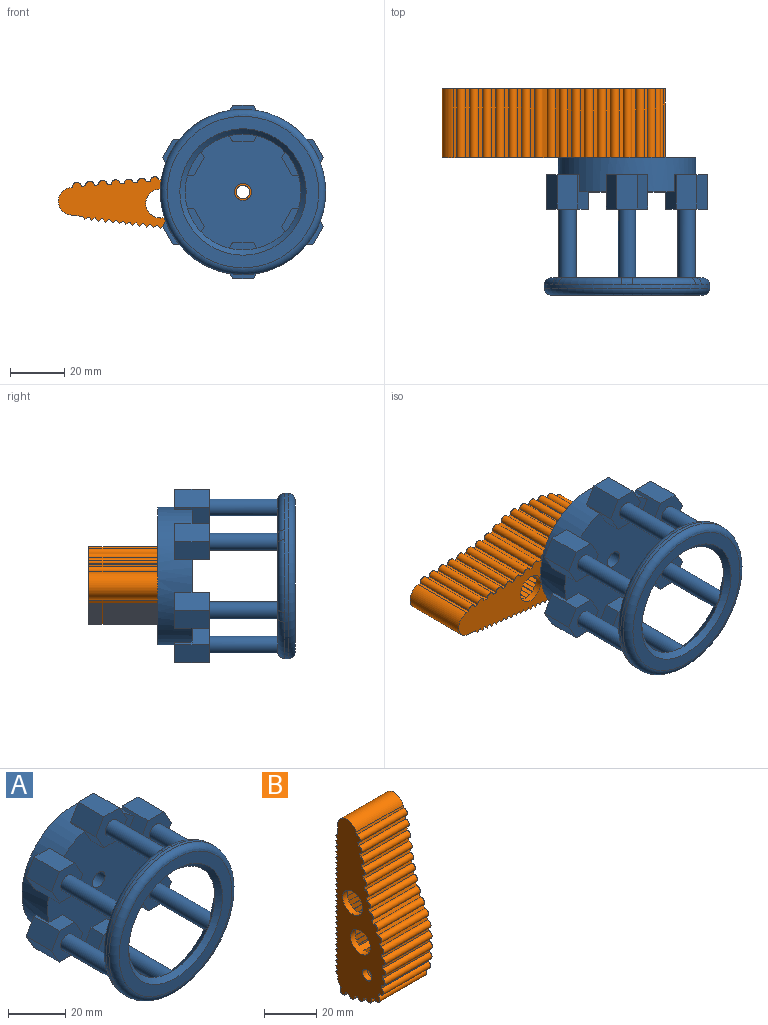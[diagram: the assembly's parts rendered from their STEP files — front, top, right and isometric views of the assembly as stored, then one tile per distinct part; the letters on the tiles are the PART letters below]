
ASSEMBLY  parts=2 mates=1
PART A: 81 faces, bbox 66.1x50.8x66.1 mm
  f0: plane 21.25x12.33mm, normal (0,1,0), area 47.9mm2, adj f18,f35,f66,f76
  f1: plane 24.54x4.17mm, normal (0,1,0), area 47.9mm2, adj f17,f18,f66,f72
  f2: plane 21.25x12.33mm, normal (0,1,0), area 47.9mm2, adj f16,f17,f66,f68
  f3: plane 21.25x12.33mm, normal (0,1,0), area 47.9mm2, adj f16,f63,f66,f69
  f4: plane 24.54x4.17mm, normal (0,1,0), area 47.9mm2, adj f63,f64,f66,f73
  f5: cylinder r=25.4mm len=50.8mm, axis (0,1,0), area 1477.3mm2, adj f6,f7,f8,f9,f15,f24,f25,f26
  f6: plane 50.8x48.77mm, normal (0,-1,0), area 1565.7mm2, adj f5,f8,f9,f13,f23,f24,f25,f28
  f7: plane 50.8x50.8mm, normal (0,1,0), area 1995.9mm2, adj f5,f80
  f8: plane 12.7x6.67mm, normal (0.87,0,0.5), area 56.4mm2, adj f5,f6,f10,f13,f14,f15
  f9: plane 12.7x7.7mm, normal (0,0,-1), area 56.4mm2, adj f5,f6,f12,f13,f14,f15
  f10: plane 12.7x7.7mm, normal (0,0,1), area 97.8mm2, adj f8,f11,f14,f15
  f11: plane 12.7x6.67mm, normal (-0.87,0,0.5), area 97.8mm2, adj f10,f12,f14,f15
  f12: plane 12.7x6.67mm, normal (-0.87,0,-0.5), area 97.8mm2, adj f9,f11,f14,f15
  f13: plane 6.67x6.35mm, normal (0.87,0,-0.5), area 48.9mm2, adj f6,f8,f9,f14
  f14: plane 15.41x13.34mm, normal (0,-1,0), area 122.5mm2, adj f8,f9,f10,f11,f12,f13,f17
  f15: plane 13.34x12.14mm, normal (0,1,0), area 82.5mm2, adj f5,f8,f9,f10,f11,f12
  f16: cylinder r=3.17mm len=29.04mm, axis (0,1,0), area 525.8mm2, adj f2,f3,f37,f66,f67
  f17: cylinder r=3.17mm len=29.04mm, axis (0,1,0), area 530.5mm2, adj f1,f2,f14,f66,f70
  f18: cylinder r=3.17mm len=29.04mm, axis (0,1,0), area 530.5mm2, adj f0,f1,f22,f66,f74
  f19: plane 12.7x6.67mm, normal (-0.87,0,-0.5), area 97.8mm2, adj f20,f21,f22,f26
  f20: plane 12.7x6.67mm, normal (-0.87,0,0.5), area 97.8mm2, adj f19,f22,f25,f26
  f21: plane 12.7x7.7mm, normal (0,0,-1), area 97.8mm2, adj f19,f22,f24,f26
  f22: plane 15.41x13.34mm, normal (0,-1,0), area 122.5mm2, adj f18,f19,f20,f21,f23,f24,f25
  f23: plane 6.67x6.35mm, normal (0.87,0,0.5), area 48.9mm2, adj f6,f22,f24,f25
  f24: plane 12.7x6.67mm, normal (0.87,0,-0.5), area 56.4mm2, adj f5,f6,f21,f22,f23,f26
  f25: plane 12.7x7.7mm, normal (0,0,1), area 56.4mm2, adj f5,f6,f20,f22,f23,f26
  f26: plane 13.34x12.14mm, normal (0,1,0), area 82.5mm2, adj f5,f19,f20,f21,f24,f25
  f27: plane 15.41x7.69mm, normal (0,1,0), area 82.5mm2, adj f5,f28,f29,f32,f33,f34
  f28: plane 12.7x6.67mm, normal (-0.87,0,0.5), area 56.4mm2, adj f5,f6,f27,f30,f31,f33
  f29: plane 12.7x6.67mm, normal (0.87,0,0.5), area 56.4mm2, adj f5,f6,f27,f30,f31,f32
  f30: plane 7.7x6.35mm, normal (0,0,1), area 48.9mm2, adj f6,f28,f29,f31
  f31: plane 15.41x13.34mm, normal (0,-1,0), area 122.5mm2, adj f28,f29,f30,f32,f33,f34,f35
  f32: plane 12.7x6.67mm, normal (0.87,0,-0.5), area 97.8mm2, adj f27,f29,f31,f34
  f33: plane 12.7x6.67mm, normal (-0.87,0,-0.5), area 97.8mm2, adj f27,f28,f31,f34
  f34: plane 12.7x7.7mm, normal (0,0,-1), area 97.8mm2, adj f27,f31,f32,f33
  f35: cylinder r=3.17mm len=29.04mm, axis (0,1,0), area 530.5mm2, adj f0,f31,f44,f66,f78
  f36: plane 15.41x7.69mm, normal (0,1,0), area 82.5mm2, adj f5,f39,f40,f41,f42,f43
  f37: plane 15.41x13.34mm, normal (0,-1,0), area 122.5mm2, adj f16,f38,f39,f40,f41,f42,f43
  f38: plane 7.7x6.35mm, normal (0,0,-1), area 48.9mm2, adj f6,f37,f42,f43
  f39: plane 12.7x6.67mm, normal (-0.87,0,0.5), area 97.8mm2, adj f36,f37,f40,f42
  f40: plane 12.7x7.7mm, normal (0,0,1), area 97.8mm2, adj f36,f37,f39,f41
  f41: plane 12.7x6.67mm, normal (0.87,0,0.5), area 97.8mm2, adj f36,f37,f40,f43
  f42: plane 12.7x6.67mm, normal (-0.87,0,-0.5), area 56.4mm2, adj f5,f6,f36,f37,f38,f39
  f43: plane 12.7x6.67mm, normal (0.87,0,-0.5), area 56.4mm2, adj f5,f6,f36,f37,f38,f41
  f44: plane 21.25x12.33mm, normal (0,1,0), area 47.9mm2, adj f35,f64,f66,f77
  f45: plane 55.95x55.95mm, normal (0,-1,0), area 750mm2, adj f65,f79
  f46: cylinder r=30.52mm len=61.03mm, axis (0,1,0), area 243.5mm2, adj f67,f68,f69,f70,f71,f72,f73,f74
  f47: plane 12.7x6.67mm, normal (0.87,0,0.5), area 97.8mm2, adj f48,f49,f50,f54
  f48: plane 12.7x7.7mm, normal (0,0,1), area 97.8mm2, adj f47,f49,f52,f54
  f49: plane 15.41x13.34mm, normal (0,-1,0), area 122.5mm2, adj f47,f48,f50,f51,f52,f53,f63
  f50: plane 12.7x6.67mm, normal (0.87,0,-0.5), area 97.8mm2, adj f47,f49,f51,f54
  f51: plane 12.7x7.7mm, normal (0,0,-1), area 56.4mm2, adj f5,f6,f49,f50,f53,f54
  f52: plane 12.7x6.67mm, normal (-0.87,0,0.5), area 56.4mm2, adj f5,f6,f48,f49,f53,f54
  f53: plane 6.67x6.35mm, normal (-0.87,0,-0.5), area 48.9mm2, adj f6,f49,f51,f52
  f54: plane 13.34x12.14mm, normal (0,1,0), area 82.5mm2, adj f5,f47,f48,f50,f51,f52
  f55: plane 12.7x6.67mm, normal (-0.87,0,-0.5), area 56.4mm2, adj f5,f6,f57,f60,f61,f62
  f56: plane 12.7x7.7mm, normal (0,0,1), area 56.4mm2, adj f5,f6,f59,f60,f61,f62
  f57: plane 12.7x7.7mm, normal (0,0,-1), area 97.8mm2, adj f55,f58,f61,f62
  f58: plane 12.7x6.67mm, normal (0.87,0,-0.5), area 97.8mm2, adj f57,f59,f61,f62
  f59: plane 12.7x6.67mm, normal (0.87,0,0.5), area 97.8mm2, adj f56,f58,f61,f62
  f60: plane 6.67x6.35mm, normal (-0.87,0,0.5), area 48.9mm2, adj f6,f55,f56,f61
  f61: plane 15.41x13.34mm, normal (0,-1,0), area 122.5mm2, adj f55,f56,f57,f58,f59,f60,f64
  f62: plane 13.34x12.14mm, normal (0,1,0), area 82.5mm2, adj f5,f55,f56,f57,f58,f59
  f63: cylinder r=3.17mm len=29.04mm, axis (0,1,0), area 530.5mm2, adj f3,f4,f49,f66,f71
  f64: cylinder r=3.17mm len=29.04mm, axis (0,1,0), area 530.5mm2, adj f4,f44,f61,f66,f75
  f65: cone r=20.78mm half-angle=45deg, axis (0,-1,0), area 378.7mm2, adj f45,f66
  f66: cone r=25.86mm half-angle=45deg, axis (0,1,0), area 778.1mm2, adj f0,f1,f2,f3,f4,f16,f17,f18
  f67: bspline ~4.25x2.61mm, area 14.8mm2, adj f16,f46,f68,f69
  f68: torus R=27.98mm, axis (0,-1,0), area 107.2mm2, adj f2,f46,f67,f70
  f69: torus R=27.98mm, axis (0,-1,0), area 107.2mm2, adj f3,f46,f67,f71
  f70: bspline ~4.79x4.23mm, area 14.8mm2, adj f17,f46,f68,f72
  f71: bspline ~4.79x4.23mm, area 14.8mm2, adj f46,f63,f69,f73
  f72: torus R=27.98mm, axis (0,-1,0), area 107.2mm2, adj f1,f46,f70,f74
  f73: torus R=27.98mm, axis (0,-1,0), area 107.2mm2, adj f4,f46,f71,f75
  f74: bspline ~4.79x4.23mm, area 14.8mm2, adj f18,f46,f72,f76
  f75: bspline ~4.79x4.23mm, area 14.8mm2, adj f46,f64,f73,f77
  f76: torus R=27.98mm, axis (0,-1,0), area 107.2mm2, adj f0,f46,f74,f78
  f77: torus R=27.98mm, axis (0,-1,0), area 107.2mm2, adj f44,f46,f75,f78
  f78: bspline ~4.25x2.61mm, area 14.8mm2, adj f35,f46,f76,f77
  f79: torus R=27.98mm, axis (0,-1,0), area 741.9mm2, adj f45,f46
  f80: cylinder r=3.14mm len=12.7mm, axis (0,-1,0), area 250.5mm2, adj f6,f7
PART B: 224 faces, bbox 25.9x27.4x83.5 mm
  f0: plane 8.1x2.64mm, normal (1,0,0), area 17.1mm2, adj f1,f4,f222,f223
  f1: extruded ~22.86x6.5mm, area 148.6mm2, adj f0,f161,f222,f223
  f2: extruded ~22.86x21.89mm, area 510.6mm2, adj f39,f161,f218,f223
  f3: extruded ~22.86x17.89mm, area 421.1mm2, adj f39,f161,f217,f222
  f4: extruded ~22.86x7.46mm, area 170.7mm2, adj f0,f7,f222,f223
  f5: extruded ~22.86x22.06mm, area 516.2mm2, adj f7,f39,f220,f223
  f6: extruded ~22.86x15.43mm, area 362mm2, adj f7,f39,f219,f222
  f7: plane 72.43x15.3mm, normal (1,0,0), area 313.8mm2, adj f4,f5,f6,f8,f9,f219,f220,f221
  f8: extruded ~71.86x22.86mm, area 1771.2mm2, adj f7,f9,f39,f219
  f9: cylinder r=2.54mm len=22.86mm, axis (-1,0,0), area 2.5mm2, adj f7,f8,f39,f220
  f10: plane 25.4x0.33mm, normal (0,1,0), area 8.4mm2, adj f38,f39,f121,f132
  f11: plane 25.4x0.33mm, normal (0,1,0), area 8.4mm2, adj f38,f39,f116,f133
  f12: plane 25.4x0.33mm, normal (0,1,0), area 8.4mm2, adj f38,f39,f129,f130
  f13: plane 25.4x0.33mm, normal (0,1,0), area 8.4mm2, adj f38,f39,f124,f131
  f14: plane 25.4x0.33mm, normal (0,1,0), area 8.4mm2, adj f38,f39,f127,f128
  f15: plane 25.4x0.33mm, normal (0,1,0), area 8.4mm2, adj f38,f39,f119,f126
  f16: plane 25.4x0.33mm, normal (0,1,0), area 8.4mm2, adj f38,f39,f122,f125
  f17: plane 25.4x0.33mm, normal (0,1,0), area 8.4mm2, adj f38,f39,f120,f123
  f18: plane 25.4x4.41mm, normal (0,1,0), area 112mm2, adj f38,f39,f63,f118
  f19: plane 25.4x0.33mm, normal (0,1,0), area 8.4mm2, adj f38,f39,f114,f117
  f20: plane 25.4x0.33mm, normal (0,1,0), area 8.4mm2, adj f38,f39,f112,f115
  f21: plane 25.4x0.33mm, normal (0,1,0), area 8.4mm2, adj f38,f39,f110,f113
  f22: plane 25.4x0.33mm, normal (0,1,0), area 8.4mm2, adj f38,f39,f108,f111
  f23: plane 25.4x0.33mm, normal (0,1,0), area 8.4mm2, adj f38,f39,f106,f109
  f24: plane 25.4x0.33mm, normal (0,1,0), area 8.4mm2, adj f38,f39,f104,f107
  f25: plane 25.4x0.33mm, normal (0,1,0), area 8.4mm2, adj f38,f39,f102,f105
  f26: plane 25.4x0.33mm, normal (0,1,0), area 8.4mm2, adj f38,f39,f100,f103
  f27: plane 25.4x0.33mm, normal (0,1,0), area 8.4mm2, adj f38,f39,f98,f101
  f28: plane 25.4x0.33mm, normal (0,1,0), area 8.4mm2, adj f38,f39,f96,f99
  f29: plane 25.4x0.33mm, normal (0,1,0), area 8.4mm2, adj f38,f39,f94,f97
  f30: plane 25.4x0.33mm, normal (0,1,0), area 8.4mm2, adj f38,f39,f92,f95
  f31: plane 25.4x0.33mm, normal (0,1,0), area 8.4mm2, adj f38,f39,f90,f93
  f32: plane 25.4x0.33mm, normal (0,1,0), area 8.4mm2, adj f38,f39,f88,f91
  f33: plane 25.4x0.33mm, normal (0,1,0), area 8.4mm2, adj f38,f39,f86,f89
  f34: plane 25.4x0.33mm, normal (0,1,0), area 8.4mm2, adj f38,f39,f84,f87
  f35: plane 25.4x0.33mm, normal (0,1,0), area 8.4mm2, adj f38,f39,f82,f85
  f36: plane 25.4x0.93mm, normal (0,1,0), area 23.6mm2, adj f38,f39,f62,f83
  f37: cylinder r=1.61mm len=25.4mm, axis (1,0,0), area 170.5mm2, adj f38,f39,f40,f62
  f38: plane 83x26.93mm, normal (-1,0,0), area 1333.9mm2, adj f10,f11,f12,f13,f14,f15,f16,f17
  f39: plane 83.1x27.04mm, normal (1,0,0), area 688.4mm2, adj f2,f3,f5,f6,f8,f9,f10,f11
  f40: cylinder r=5.08mm len=25.4mm, axis (-1,0,0), area 26.9mm2, adj f37,f38,f39,f61
  f41: cylinder r=1.61mm len=25.4mm, axis (1,0,0), area 125.2mm2, adj f38,f39,f42,f46
  f42: extruded ~25.4x1.57mm, area 40.3mm2, adj f38,f39,f41,f79
  f43: extruded ~25.4x1.01mm, area 26.7mm2, adj f38,f39,f63,f81
  f44: extruded ~25.4x1.55mm, area 40.3mm2, adj f38,f39,f80,f81
  f45: extruded ~25.4x1.56mm, area 40.3mm2, adj f38,f39,f79,f80
  f46: extruded ~25.4x1.57mm, area 40.4mm2, adj f38,f39,f41,f78
  f47: extruded ~25.4x1.56mm, area 40.4mm2, adj f38,f39,f77,f78
  f48: extruded ~25.4x1.55mm, area 40.5mm2, adj f38,f39,f76,f77
  f49: extruded ~25.4x1.5mm, area 40.7mm2, adj f38,f39,f75,f76
  f50: extruded ~25.4x1.43mm, area 40.9mm2, adj f38,f39,f74,f75
  f51: extruded ~25.4x1.43mm, area 40.4mm2, adj f38,f39,f73,f74
  f52: extruded ~25.4x1.54mm, area 40.5mm2, adj f38,f39,f72,f73
  f53: extruded ~25.4x1.58mm, area 40.4mm2, adj f38,f39,f71,f72
  f54: extruded ~25.4x1.59mm, area 40.3mm2, adj f38,f39,f70,f71
  f55: extruded ~25.4x1.58mm, area 40.3mm2, adj f38,f39,f69,f70
  f56: extruded ~25.4x1.56mm, area 40.3mm2, adj f38,f39,f68,f69
  f57: extruded ~25.4x1.42mm, area 40.6mm2, adj f38,f39,f67,f68
  f58: extruded ~25.4x1.48mm, area 43.8mm2, adj f38,f39,f66,f67
  f59: extruded ~25.4x1.5mm, area 40.9mm2, adj f38,f39,f65,f66
  f60: extruded ~25.4x1.54mm, area 40.3mm2, adj f38,f39,f64,f65
  f61: extruded ~25.4x0.54mm, area 13.7mm2, adj f38,f39,f40,f64
  f62: cylinder r=5.08mm len=25.4mm, axis (-1,0,0), area 117mm2, adj f36,f37,f38,f39
  f63: cylinder r=5.08mm len=25.4mm, axis (-1,0,0), area 368.5mm2, adj f18,f38,f39,f43
  f64: cylinder r=1.61mm len=25.4mm, axis (1,0,0), area 132.7mm2, adj f38,f39,f60,f61
  f65: cylinder r=1.61mm len=25.4mm, axis (1,0,0), area 129.9mm2, adj f38,f39,f59,f60
  f66: cylinder r=1.61mm len=25.4mm, axis (1,0,0), area 138.6mm2, adj f38,f39,f58,f59
  f67: cylinder r=1.61mm len=25.4mm, axis (1,0,0), area 154.1mm2, adj f38,f39,f57,f58
  f68: cylinder r=1.61mm len=25.4mm, axis (1,0,0), area 136.1mm2, adj f38,f39,f56,f57
  f69: cylinder r=1.61mm len=25.4mm, axis (1,0,0), area 130.7mm2, adj f38,f39,f55,f56
  f70: cylinder r=1.61mm len=25.4mm, axis (1,0,0), area 129.5mm2, adj f38,f39,f54,f55
  f71: cylinder r=1.61mm len=25.4mm, axis (1,0,0), area 129.9mm2, adj f38,f39,f53,f54
  f72: cylinder r=1.61mm len=25.4mm, axis (1,0,0), area 132.8mm2, adj f38,f39,f52,f53
  f73: cylinder r=1.61mm len=25.4mm, axis (1,0,0), area 134.4mm2, adj f38,f39,f51,f52
  f74: cylinder r=1.61mm len=25.4mm, axis (1,0,0), area 123.2mm2, adj f38,f39,f50,f51
  f75: cylinder r=1.61mm len=25.4mm, axis (1,0,0), area 117.6mm2, adj f38,f39,f49,f50
  f76: cylinder r=1.61mm len=25.4mm, axis (1,0,0), area 120.7mm2, adj f38,f39,f48,f49
  f77: cylinder r=1.61mm len=25.4mm, axis (1,0,0), area 123.3mm2, adj f38,f39,f47,f48
  f78: cylinder r=1.61mm len=25.4mm, axis (1,0,0), area 124.4mm2, adj f38,f39,f46,f47
  f79: cylinder r=1.61mm len=25.4mm, axis (1,0,0), area 126mm2, adj f38,f39,f42,f45
  f80: cylinder r=1.61mm len=25.4mm, axis (1,0,0), area 127mm2, adj f38,f39,f44,f45
  f81: cylinder r=1.61mm len=25.4mm, axis (1,0,0), area 129.2mm2, adj f38,f39,f43,f44
  f82: plane 25.4x1.11mm, normal (0,0.72,0.7), area 39.2mm2, adj f35,f38,f39,f83
  f83: plane 25.4x1.11mm, normal (0,0.72,-0.7), area 39.2mm2, adj f36,f38,f39,f82
  f84: plane 25.4x1.11mm, normal (0,0.72,0.7), area 39.2mm2, adj f34,f38,f39,f85
  f85: plane 25.4x1.11mm, normal (0,0.72,-0.7), area 39.2mm2, adj f35,f38,f39,f84
  f86: plane 25.4x1.11mm, normal (0,0.72,0.7), area 39.2mm2, adj f33,f38,f39,f87
  f87: plane 25.4x1.11mm, normal (0,0.72,-0.7), area 39.2mm2, adj f34,f38,f39,f86
  f88: plane 25.4x1.11mm, normal (0,0.72,0.7), area 39.2mm2, adj f32,f38,f39,f89
  f89: plane 25.4x1.11mm, normal (0,0.72,-0.7), area 39.2mm2, adj f33,f38,f39,f88
  f90: plane 25.4x1.11mm, normal (0,0.72,0.7), area 39.2mm2, adj f31,f38,f39,f91
  f91: plane 25.4x1.11mm, normal (0,0.72,-0.7), area 39.2mm2, adj f32,f38,f39,f90
  f92: plane 25.4x1.11mm, normal (0,0.72,0.7), area 39.2mm2, adj f30,f38,f39,f93
  f93: plane 25.4x1.11mm, normal (0,0.72,-0.7), area 39.2mm2, adj f31,f38,f39,f92
  f94: plane 25.4x1.11mm, normal (0,0.72,0.7), area 39.2mm2, adj f29,f38,f39,f95
  f95: plane 25.4x1.11mm, normal (0,0.72,-0.7), area 39.2mm2, adj f30,f38,f39,f94
  f96: plane 25.4x1.11mm, normal (0,0.72,0.7), area 39.2mm2, adj f28,f38,f39,f97
  f97: plane 25.4x1.11mm, normal (0,0.72,-0.7), area 39.2mm2, adj f29,f38,f39,f96
  f98: plane 25.4x1.11mm, normal (0,0.72,0.7), area 39.2mm2, adj f27,f38,f39,f99
  f99: plane 25.4x1.11mm, normal (0,0.72,-0.7), area 39.2mm2, adj f28,f38,f39,f98
  f100: plane 25.4x1.11mm, normal (0,0.72,0.7), area 39.2mm2, adj f26,f38,f39,f101
  f101: plane 25.4x1.11mm, normal (0,0.72,-0.7), area 39.2mm2, adj f27,f38,f39,f100
  f102: plane 25.4x1.11mm, normal (0,0.72,0.7), area 39.2mm2, adj f25,f38,f39,f103
  f103: plane 25.4x1.11mm, normal (0,0.72,-0.7), area 39.2mm2, adj f26,f38,f39,f102
  f104: plane 25.4x1.11mm, normal (0,0.72,0.7), area 39.2mm2, adj f24,f38,f39,f105
  f105: plane 25.4x1.11mm, normal (0,0.72,-0.7), area 39.2mm2, adj f25,f38,f39,f104
  f106: plane 25.4x1.11mm, normal (0,0.72,0.7), area 39.2mm2, adj f23,f38,f39,f107
  f107: plane 25.4x1.11mm, normal (0,0.72,-0.7), area 39.2mm2, adj f24,f38,f39,f106
  f108: plane 25.4x1.11mm, normal (0,0.72,0.7), area 39.2mm2, adj f22,f38,f39,f109
  f109: plane 25.4x1.11mm, normal (0,0.72,-0.7), area 39.2mm2, adj f23,f38,f39,f108
  f110: plane 25.4x1.11mm, normal (0,0.72,0.7), area 39.2mm2, adj f21,f38,f39,f111
  f111: plane 25.4x1.11mm, normal (0,0.72,-0.7), area 39.2mm2, adj f22,f38,f39,f110
  f112: plane 25.4x1.11mm, normal (0,0.72,0.7), area 39.2mm2, adj f20,f38,f39,f113
  f113: plane 25.4x1.11mm, normal (0,0.72,-0.7), area 39.2mm2, adj f21,f38,f39,f112
  f114: plane 25.4x1.11mm, normal (0,0.72,0.7), area 39.2mm2, adj f19,f38,f39,f115
  f115: plane 25.4x1.11mm, normal (0,0.72,-0.7), area 39.2mm2, adj f20,f38,f39,f114
  f116: plane 25.4x1.11mm, normal (0,0.72,0.7), area 39.2mm2, adj f11,f38,f39,f117
  f117: plane 25.4x1.11mm, normal (0,0.72,-0.7), area 39.2mm2, adj f19,f38,f39,f116
  f118: plane 25.4x1.11mm, normal (0,0.72,0.7), area 39.2mm2, adj f18,f38,f39,f119
  f119: plane 25.4x1.11mm, normal (0,0.72,-0.7), area 39.2mm2, adj f15,f38,f39,f118
  f120: plane 25.4x1.11mm, normal (0,0.72,0.7), area 39.2mm2, adj f17,f38,f39,f121
  f121: plane 25.4x1.11mm, normal (0,0.72,-0.7), area 39.2mm2, adj f10,f38,f39,f120
  f122: plane 25.4x1.11mm, normal (0,0.72,0.7), area 39.2mm2, adj f16,f38,f39,f123
  f123: plane 25.4x1.11mm, normal (0,0.72,-0.7), area 39.2mm2, adj f17,f38,f39,f122
  f124: plane 25.4x1.11mm, normal (0,0.72,0.7), area 39.2mm2, adj f13,f38,f39,f125
  f125: plane 25.4x1.11mm, normal (0,0.72,-0.7), area 39.2mm2, adj f16,f38,f39,f124
  f126: plane 25.4x1.11mm, normal (0,0.72,0.7), area 39.2mm2, adj f15,f38,f39,f127
  f127: plane 25.4x1.11mm, normal (0,0.72,-0.7), area 39.2mm2, adj f14,f38,f39,f126
  f128: plane 25.4x1.11mm, normal (0,0.72,0.7), area 39.2mm2, adj f14,f38,f39,f129
  f129: plane 25.4x1.11mm, normal (0,0.72,-0.7), area 39.2mm2, adj f12,f38,f39,f128
  f130: plane 25.4x1.11mm, normal (0,0.72,0.7), area 39.2mm2, adj f12,f38,f39,f131
  f131: plane 25.4x1.11mm, normal (0,0.72,-0.7), area 39.2mm2, adj f13,f38,f39,f130
  f132: plane 25.4x1.11mm, normal (0,0.72,0.7), area 39.2mm2, adj f10,f38,f39,f133
  f133: plane 25.4x1.11mm, normal (0,0.72,-0.7), area 39.2mm2, adj f11,f38,f39,f132
  f134: plane 22.86x2.4mm, normal (0,-1,0), area 54.8mm2, adj f39,f161,f204,f215
  f135: plane 22.86x2.4mm, normal (0,-1,0), area 54.8mm2, adj f39,f161,f199,f216
  f136: plane 22.86x2.4mm, normal (0,-1,0), area 54.8mm2, adj f39,f161,f212,f213
  f137: plane 22.86x2.4mm, normal (0,-1,0), area 54.8mm2, adj f39,f161,f207,f214
  f138: plane 22.86x2.4mm, normal (0,-1,0), area 54.8mm2, adj f39,f161,f210,f211
  f139: plane 22.86x2.4mm, normal (0,-1,0), area 54.8mm2, adj f39,f161,f202,f209
  f140: plane 22.86x2.4mm, normal (0,-1,0), area 54.8mm2, adj f39,f161,f205,f208
  f141: plane 22.86x2.4mm, normal (0,-1,0), area 54.8mm2, adj f39,f161,f203,f206
  f142: plane 22.86x5.44mm, normal (0,-1,0), area 124.4mm2, adj f39,f161,f164,f201
  f143: plane 22.86x2.4mm, normal (0,-1,0), area 54.8mm2, adj f39,f161,f197,f200
  f144: plane 22.86x2.4mm, normal (0,-1,0), area 54.8mm2, adj f39,f161,f195,f198
  f145: plane 22.86x2.4mm, normal (0,-1,0), area 54.8mm2, adj f39,f161,f193,f196
  f146: plane 22.86x2.4mm, normal (0,-1,0), area 54.8mm2, adj f39,f161,f191,f194
  f147: plane 22.86x2.4mm, normal (0,-1,0), area 54.8mm2, adj f39,f161,f189,f192
  f148: plane 22.86x2.4mm, normal (0,-1,0), area 54.8mm2, adj f39,f161,f187,f190
  f149: plane 22.86x2.4mm, normal (0,-1,0), area 54.8mm2, adj f39,f161,f185,f188
  f150: plane 22.86x2.4mm, normal (0,-1,0), area 54.8mm2, adj f39,f161,f183,f186
  f151: plane 22.86x2.4mm, normal (0,-1,0), area 54.8mm2, adj f39,f161,f181,f184
  f152: plane 22.86x2.4mm, normal (0,-1,0), area 54.8mm2, adj f39,f161,f179,f182
  f153: plane 22.86x2.4mm, normal (0,-1,0), area 54.8mm2, adj f39,f161,f177,f180
  f154: plane 22.86x2.4mm, normal (0,-1,0), area 54.8mm2, adj f39,f161,f175,f178
  f155: plane 22.86x2.4mm, normal (0,-1,0), area 54.8mm2, adj f39,f161,f173,f176
  f156: plane 22.86x2.4mm, normal (0,-1,0), area 54.8mm2, adj f39,f161,f171,f174
  f157: plane 22.86x2.4mm, normal (0,-1,0), area 54.8mm2, adj f39,f161,f169,f172
  f158: plane 22.86x2.4mm, normal (0,-1,0), area 54.8mm2, adj f39,f161,f167,f170
  f159: plane 22.86x2.4mm, normal (0,-1,0), area 54.8mm2, adj f39,f161,f165,f168
  f160: plane 22.86x1.96mm, normal (0,-1,0), area 44.9mm2, adj f39,f161,f163,f166
  f161: plane 76.52x9.84mm, normal (1,0,0), area 314.6mm2, adj f1,f2,f3,f134,f135,f136,f137,f138
  f162: extruded ~22.86x6.58mm, area 154.7mm2, adj f39,f161,f163,f217
  f163: cylinder r=2.54mm len=22.86mm, axis (-1,0,0), area 97.2mm2, adj f39,f160,f161,f162
  f164: cylinder r=2.54mm len=22.86mm, axis (-1,0,0), area 91mm2, adj f39,f142,f161,f218
  f165: plane 22.86x0.07mm, normal (0,-0.72,-0.7), area 2.3mm2, adj f39,f159,f161,f166
  f166: plane 22.86x0.07mm, normal (0,-0.72,0.7), area 2.3mm2, adj f39,f160,f161,f165
  f167: plane 22.86x0.07mm, normal (0,-0.72,-0.7), area 2.3mm2, adj f39,f158,f161,f168
  f168: plane 22.86x0.07mm, normal (0,-0.72,0.7), area 2.3mm2, adj f39,f159,f161,f167
  f169: plane 22.86x0.07mm, normal (0,-0.72,-0.7), area 2.3mm2, adj f39,f157,f161,f170
  f170: plane 22.86x0.07mm, normal (0,-0.72,0.7), area 2.3mm2, adj f39,f158,f161,f169
  f171: plane 22.86x0.07mm, normal (0,-0.72,-0.7), area 2.3mm2, adj f39,f156,f161,f172
  f172: plane 22.86x0.07mm, normal (0,-0.72,0.7), area 2.3mm2, adj f39,f157,f161,f171
  f173: plane 22.86x0.07mm, normal (0,-0.72,-0.7), area 2.3mm2, adj f39,f155,f161,f174
  f174: plane 22.86x0.07mm, normal (0,-0.72,0.7), area 2.3mm2, adj f39,f156,f161,f173
  f175: plane 22.86x0.07mm, normal (0,-0.72,-0.7), area 2.3mm2, adj f39,f154,f161,f176
  f176: plane 22.86x0.07mm, normal (0,-0.72,0.7), area 2.3mm2, adj f39,f155,f161,f175
  f177: plane 22.86x0.07mm, normal (0,-0.72,-0.7), area 2.3mm2, adj f39,f153,f161,f178
  f178: plane 22.86x0.07mm, normal (0,-0.72,0.7), area 2.3mm2, adj f39,f154,f161,f177
  f179: plane 22.86x0.07mm, normal (0,-0.72,-0.7), area 2.3mm2, adj f39,f152,f161,f180
  f180: plane 22.86x0.07mm, normal (0,-0.72,0.7), area 2.3mm2, adj f39,f153,f161,f179
  f181: plane 22.86x0.07mm, normal (0,-0.72,-0.7), area 2.3mm2, adj f39,f151,f161,f182
  f182: plane 22.86x0.07mm, normal (0,-0.72,0.7), area 2.3mm2, adj f39,f152,f161,f181
  f183: plane 22.86x0.07mm, normal (0,-0.72,-0.7), area 2.3mm2, adj f39,f150,f161,f184
  f184: plane 22.86x0.07mm, normal (0,-0.72,0.7), area 2.3mm2, adj f39,f151,f161,f183
  f185: plane 22.86x0.07mm, normal (0,-0.72,-0.7), area 2.3mm2, adj f39,f149,f161,f186
  f186: plane 22.86x0.07mm, normal (0,-0.72,0.7), area 2.3mm2, adj f39,f150,f161,f185
  f187: plane 22.86x0.07mm, normal (0,-0.72,-0.7), area 2.3mm2, adj f39,f148,f161,f188
  f188: plane 22.86x0.07mm, normal (0,-0.72,0.7), area 2.3mm2, adj f39,f149,f161,f187
  f189: plane 22.86x0.07mm, normal (0,-0.72,-0.7), area 2.3mm2, adj f39,f147,f161,f190
  f190: plane 22.86x0.07mm, normal (0,-0.72,0.7), area 2.3mm2, adj f39,f148,f161,f189
  f191: plane 22.86x0.07mm, normal (0,-0.72,-0.7), area 2.3mm2, adj f39,f146,f161,f192
  f192: plane 22.86x0.07mm, normal (0,-0.72,0.7), area 2.3mm2, adj f39,f147,f161,f191
  f193: plane 22.86x0.07mm, normal (0,-0.72,-0.7), area 2.3mm2, adj f39,f145,f161,f194
  f194: plane 22.86x0.07mm, normal (0,-0.72,0.7), area 2.3mm2, adj f39,f146,f161,f193
  f195: plane 22.86x0.07mm, normal (0,-0.72,-0.7), area 2.3mm2, adj f39,f144,f161,f196
  f196: plane 22.86x0.07mm, normal (0,-0.72,0.7), area 2.3mm2, adj f39,f145,f161,f195
  f197: plane 22.86x0.07mm, normal (0,-0.72,-0.7), area 2.3mm2, adj f39,f143,f161,f198
  f198: plane 22.86x0.07mm, normal (0,-0.72,0.7), area 2.3mm2, adj f39,f144,f161,f197
  f199: plane 22.86x0.07mm, normal (0,-0.72,-0.7), area 2.3mm2, adj f39,f135,f161,f200
  f200: plane 22.86x0.07mm, normal (0,-0.72,0.7), area 2.3mm2, adj f39,f143,f161,f199
  f201: plane 22.86x0.07mm, normal (0,-0.72,-0.7), area 2.3mm2, adj f39,f142,f161,f202
  f202: plane 22.86x0.07mm, normal (0,-0.72,0.7), area 2.3mm2, adj f39,f139,f161,f201
  f203: plane 22.86x0.07mm, normal (0,-0.72,-0.7), area 2.3mm2, adj f39,f141,f161,f204
  f204: plane 22.86x0.07mm, normal (0,-0.72,0.7), area 2.3mm2, adj f39,f134,f161,f203
  f205: plane 22.86x0.07mm, normal (0,-0.72,-0.7), area 2.3mm2, adj f39,f140,f161,f206
  f206: plane 22.86x0.07mm, normal (0,-0.72,0.7), area 2.3mm2, adj f39,f141,f161,f205
  f207: plane 22.86x0.07mm, normal (0,-0.72,-0.7), area 2.3mm2, adj f39,f137,f161,f208
  f208: plane 22.86x0.07mm, normal (0,-0.72,0.7), area 2.3mm2, adj f39,f140,f161,f207
  f209: plane 22.86x0.07mm, normal (0,-0.72,-0.7), area 2.3mm2, adj f39,f139,f161,f210
  f210: plane 22.86x0.07mm, normal (0,-0.72,0.7), area 2.3mm2, adj f39,f138,f161,f209
  f211: plane 22.86x0.07mm, normal (0,-0.72,-0.7), area 2.3mm2, adj f39,f138,f161,f212
  f212: plane 22.86x0.07mm, normal (0,-0.72,0.7), area 2.3mm2, adj f39,f136,f161,f211
  f213: plane 22.86x0.07mm, normal (0,-0.72,-0.7), area 2.3mm2, adj f39,f136,f161,f214
  f214: plane 22.86x0.07mm, normal (0,-0.72,0.7), area 2.3mm2, adj f39,f137,f161,f213
  f215: plane 22.86x0.07mm, normal (0,-0.72,-0.7), area 2.3mm2, adj f39,f134,f161,f216
  f216: plane 22.86x0.07mm, normal (0,-0.72,0.7), area 2.3mm2, adj f39,f135,f161,f215
  f217: plane 22.86x1.08mm, normal (0,0.8,-0.6), area 30.7mm2, adj f3,f39,f161,f162
  f218: plane 22.86x7.76mm, normal (0,1,0.08), area 177.9mm2, adj f2,f39,f161,f164
  f219: plane 22.86x1.68mm, normal (0,-0.8,0.6), area 47.7mm2, adj f6,f7,f8,f39
  f220: plane 22.86x6.23mm, normal (0,-1,-0.08), area 142.9mm2, adj f5,f7,f9,f39
  f221: cylinder r=2.47mm len=4.93mm, axis (1,0,0), area 39.3mm2, adj f7,f38
  f222: cylinder r=5.36mm len=25.4mm, axis (-1,0,0), area 208mm2, adj f0,f1,f3,f4,f6,f7,f38,f39
  f223: cylinder r=5.36mm len=25.4mm, axis (-1,0,0), area 219.7mm2, adj f0,f1,f2,f4,f5,f7,f38,f39
PLACE A t=(-10.85,3.09,-9.07)mm fixed
PLACE B rot(axis=(-0.55,-0.55,0.62),116.1deg) t=(-159.47,3.09,-7.38)mm
MATE revolute A.f5 <-> B.f221  axis (0,1,0) through (-10.85,3.09,-9.07)mm
